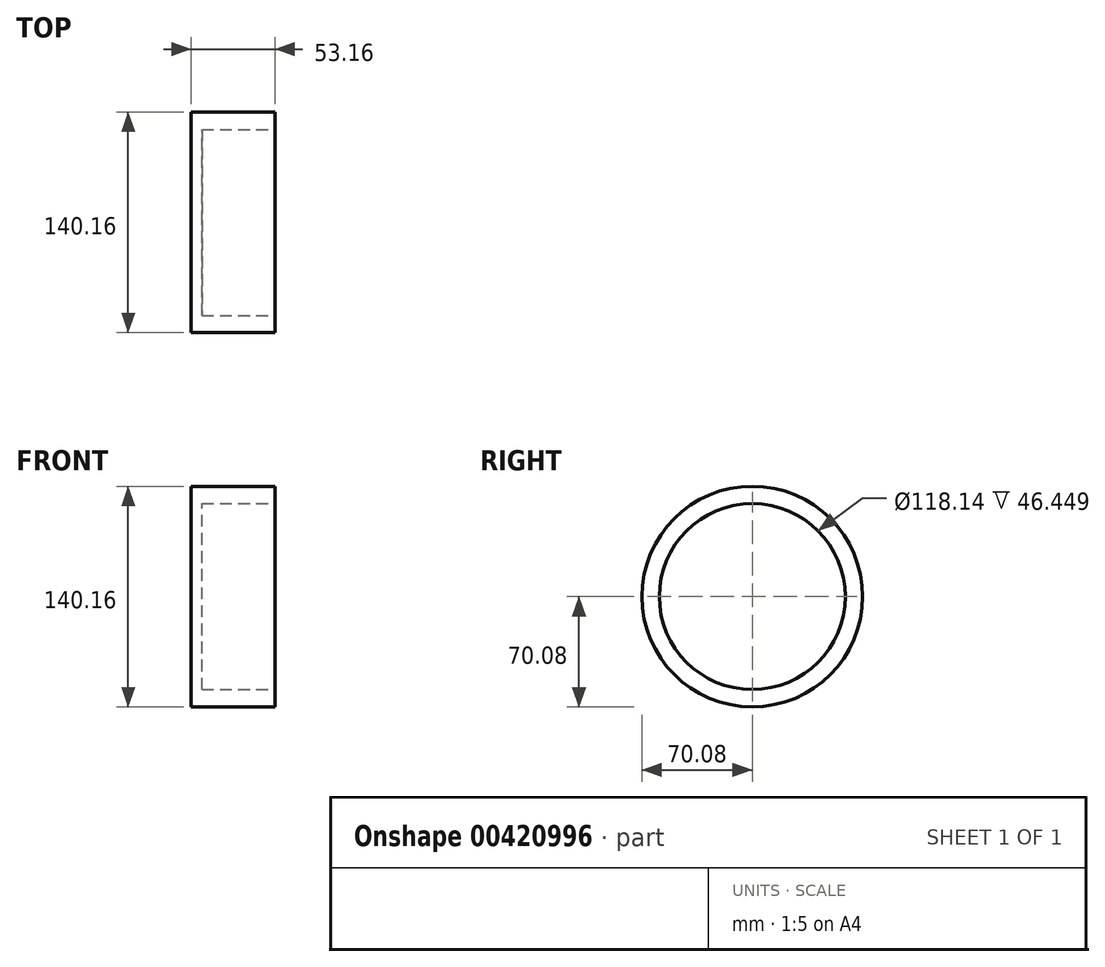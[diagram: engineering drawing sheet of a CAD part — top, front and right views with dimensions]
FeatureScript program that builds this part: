
annotation { "Feature Type Name" : "Feature", "Feature Type Description" : "" }
export const myFeature = defineFeature(function(context is Context, id is Id, definition is map)
    precondition{}
    {
        {
            var Q0;
            Q0=qCreatedBy(makeId("Front.planeOp"),FACE);
            var sketch = newSketch(context, id + "F0", { "sketchPlane" : qUnion([Q0])});
            skLineSegment(sketch, "E0", {"start": v(0, 0) * mm, "end": v(0, 70.08) * mm});
            skLineSegment(sketch, "E1", {"start": v(0, 70.08) * mm, "end": v(53.16, 70.08) * mm});
            skLineSegment(sketch, "E2", {"start": v(53.16, 70.08) * mm, "end": v(53.16, 59.07) * mm});
            skLineSegment(sketch, "E3", {"start": v(53.16, 59.07) * mm, "end": v(6.71, 59.07) * mm});
            skLineSegment(sketch, "E4", {"start": v(6.71, 59.07) * mm, "end": v(6.71, 0) * mm});
            skLineSegment(sketch, "E5", {"start": v(6.71, 0) * mm, "end": v(0, 0) * mm});
            skSolve(sketch);
        }
        {
            var Q0;
            Q0=makeQuery(id+"F0.imprint","IMPRINT",FACE,{"disambiguationData":[TD([[makeQuery(id+"F0.imprint","IMPRINT",EDGE,{"derivedFrom":sQuery(id+"F0.wireOp",EDGE,"E0")}),-1.0]])]});
            var Q1;
            Q1=sQuery(id+"F0.wireOp",EDGE,"E5");
            revolve(context, id + "F1", {"entities" : qUnion([Q0]), "axis" : qUnion([Q1]), "revolveType" : RevolveType.FULL});
        }
    });
